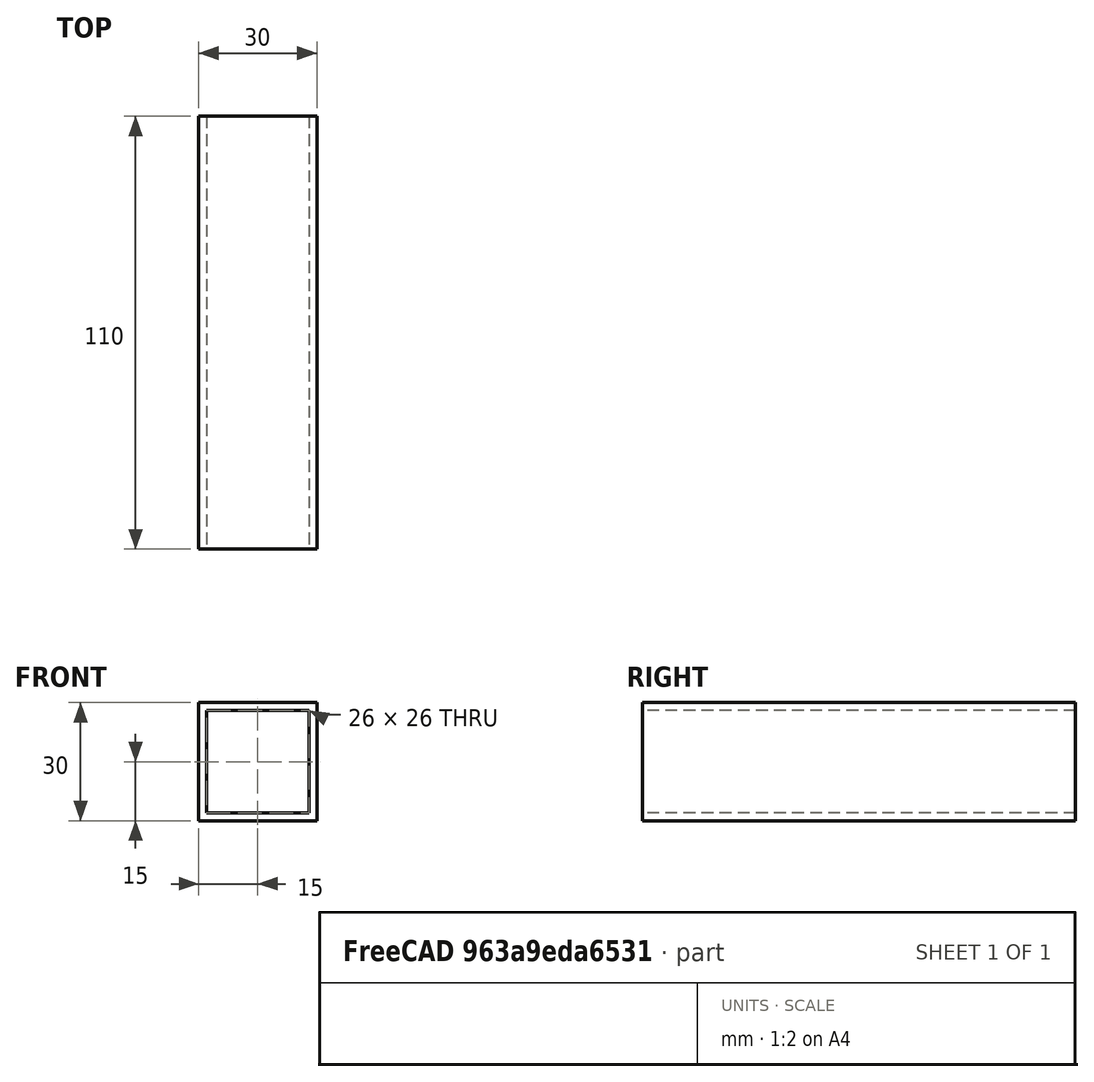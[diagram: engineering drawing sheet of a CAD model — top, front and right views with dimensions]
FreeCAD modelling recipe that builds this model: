
FCSTD DOCUMENT  (FreeCAD 0.20R29603 (Git))
Label: AluProfil 30x30x2_quer_kurz
License: All rights reserved
LicenseURL: http://en.wikipedia.org/wiki/All_rights_reserved
objects: Sketcher::SketchObject×1, PartDesign::Pad×1, PartDesign::Body×1
note: 4 computed .brp shape members not serialized (recipe doc carries the construction recipe); baked Part::Feature solids carry a one-line shape summary decoded from their .brp

FEATURE [Sketcher::SketchObject] Sketch001
  FullyConstrained = true
  MapMode = 5
  Placement = pos=(0,0,0) rot=(1,0,0;1.5708rad)
  Support = -> [XZ_Plane001]
  sketch-geometry (8):
    g0: LineSegment StartX=0 StartY=0 StartZ=0 EndX=30 EndY=0 EndZ=0
    g1: LineSegment StartX=30 StartY=0 StartZ=0 EndX=30 EndY=-30 EndZ=0
    g2: LineSegment StartX=30 StartY=-30 StartZ=0 EndX=0 EndY=-30 EndZ=0
    g3: LineSegment StartX=0 StartY=-30 StartZ=0 EndX=0 EndY=0 EndZ=0
    g4: LineSegment StartX=2 StartY=-2 StartZ=0 EndX=28 EndY=-2 EndZ=0
    g5: LineSegment StartX=28 StartY=-2 StartZ=0 EndX=28 EndY=-28 EndZ=0
    g6: LineSegment StartX=28 StartY=-28 StartZ=0 EndX=2 EndY=-28 EndZ=0
    g7: LineSegment StartX=2 StartY=-28 StartZ=0 EndX=2 EndY=-2 EndZ=0
  constraints (24):
    c: Coincident(g0,g1)
    c: Coincident(g1,g2)
    c: Coincident(g2,g3)
    c: Coincident(g3,g0)
    c: Horizontal(g0)
    c: Horizontal(g2)
    c: Vertical(g1)
    c: Vertical(g3)
    c: PointOnObject(g0,g-2)
    c: Coincident(g4,g5)
    c: Coincident(g5,g6)
    c: Coincident(g6,g7)
    c: Coincident(g7,g4)
    c: Horizontal(g4)
    c: Horizontal(g6)
    c: Vertical(g5)
    c: Vertical(g7)
    c: Distance(g0) = 30
    c: Distance(g1) = 30
    c: Distance(g4) = 26
    c: Distance(g5) = 26
    c: Distance(g2,g7) = 2
    c: Distance(g4,g0) = 2
    c: PointOnObject(g0,g-1)
FEATURE [PartDesign::Pad] Pad001  label="länge 840mm"
  Direction = (0,-1,-2e-16)
  Length = 110
  Length2 = 10
  Placement = pos=(0,0,0) rot=(1,0,0;1.5708rad)
  Profile = -> Sketch001
  ReferenceAxis = -> Sketch001 [N_Axis]
  Type = 0
FEATURE [PartDesign::Body] Body001  label="AluProfil 30x30x2 002"
  Group = -> [Sketch001,Pad001]
  Origin = -> Origin001
  Placement = pos=(-240,390,0) rot=(0,0,1;0rad)
  Tip = -> Pad001
